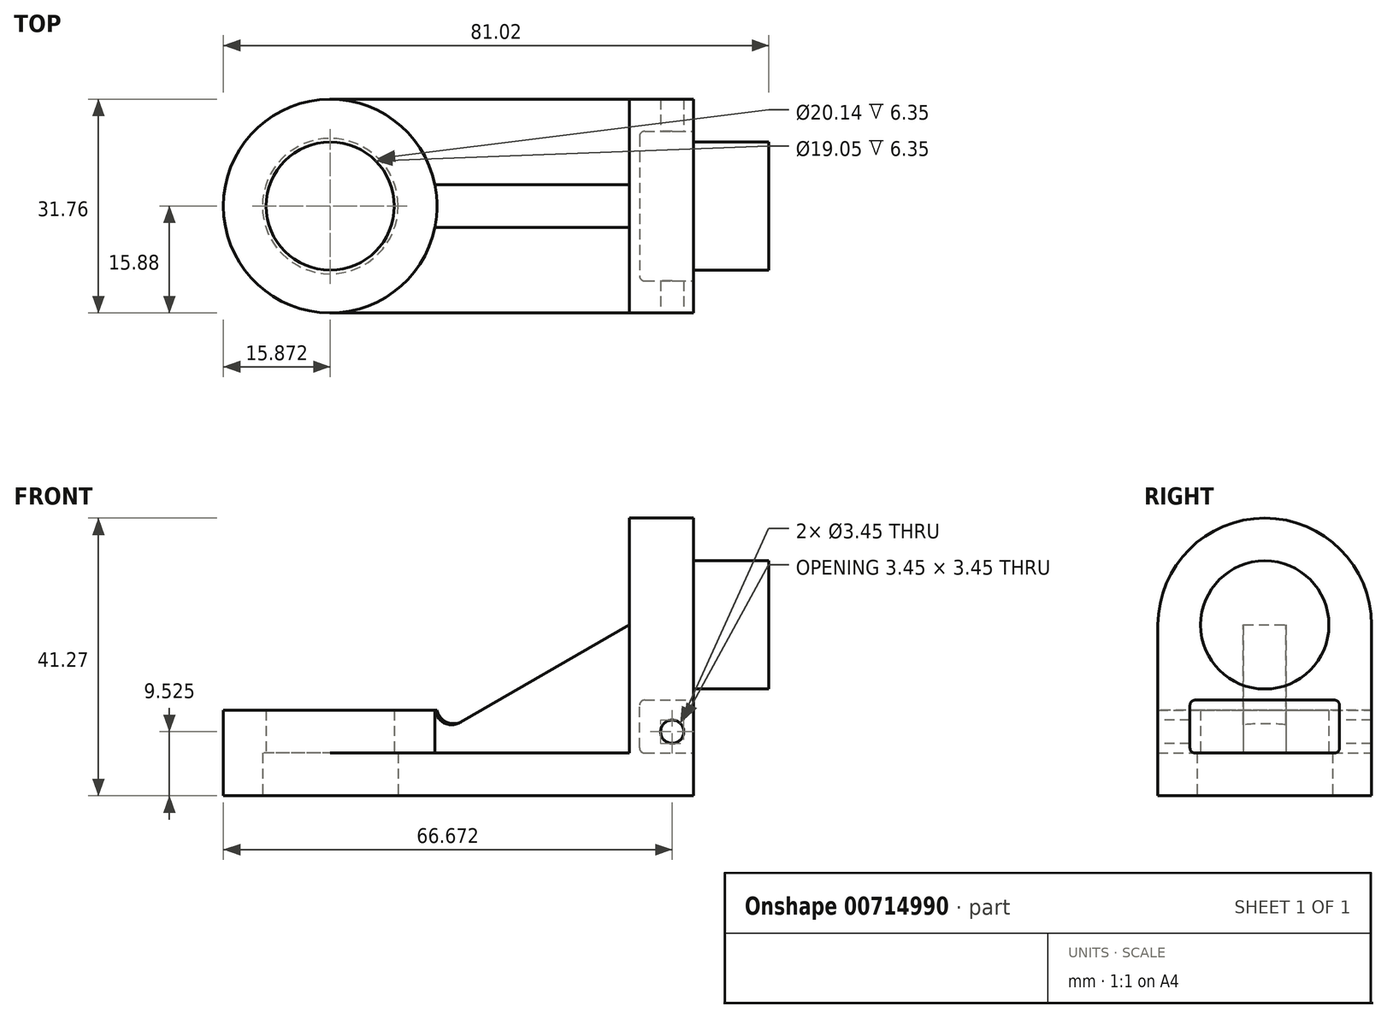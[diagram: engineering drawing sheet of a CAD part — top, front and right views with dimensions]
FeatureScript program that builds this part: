
annotation { "Feature Type Name" : "Feature", "Feature Type Description" : "" }
export const myFeature = defineFeature(function(context is Context, id is Id, definition is map)
    precondition{}
    {
        {
            var Q0;
            Q0=qCreatedBy(makeId("Top.planeOp"),FACE);
            var sketch = newSketch(context, id + "F0", { "sketchPlane" : qUnion([Q0])});
            skLineSegment(sketch, "E0.bottom", {"start": v(26.99, -15.88) * mm, "end": v(-26.99, -15.88) * mm});
            skLineSegment(sketch, "E0.top", {"start": v(26.99, 15.88) * mm, "end": v(-26.99, 15.87) * mm});
            skLineSegment(sketch, "E0.left", {"start": v(26.99, -15.88) * mm, "end": v(26.99, 15.88) * mm});
            skPoint(sketch, "E0.middle", {"position": v(0, 0) * mm});
            skArc(sketch, "E1", {"start": v(-26.99, 15.87) * mm, "mid": v(-42.86, 0) * mm, "end": v(-26.99, -15.87) * mm});
            skCircle(sketch, "E2", {"center": v(-26.99, 0) * mm, "radius": 10.07 * mm});
            skSolve(sketch);
        }
        {
            var Q0;
            Q0 = qSketchRegion(id + "F0", true);
            extrude(context, id + "F1", {"entities" : qUnion([Q0]), "depth" : 6.35 * mm, "offsetDistance" : 25.4 * mm});
        }
        {
            var Q0;
            Q0=makeQuery(id+"F1.opExtrude","CAP_FACE",FACE,{"disambiguationData":[OSD([sQuery(id+"F0.wireOp",EDGE,"E0.bottom"),sQuery(id+"F0.wireOp",EDGE,"E0.top"),sQuery(id+"F0.wireOp",EDGE,"E0.left"),sQuery(id+"F0.wireOp",EDGE,"E1")])],"isStart":false});
            var sketch = newSketch(context, id + "F2", { "sketchPlane" : qUnion([Q0])});
            skCircle(sketch, "E3", {"center": v(-26.99, 0) * mm, "radius": 9.53 * mm});
            skCircle(sketch, "E4", {"center": v(-26.99, 0) * mm, "radius": 15.88 * mm});
            skSolve(sketch);
        }
        {
            var Q0;
            Q0 = qSketchRegion(id + "F2", true);
            extrude(context, id + "F3", {"entities" : qUnion([Q0]), "operationType" : NewBodyOperationType.ADD, "depth" : 6.35 * mm, "offsetDistance" : 25.4 * mm});
        }
        {
            var Q0;
            Q0=makeQuery(id+"F1.opExtrude","CAP_FACE",FACE,{"disambiguationData":[OSD([sQuery(id+"F0.wireOp",EDGE,"E0.bottom"),sQuery(id+"F0.wireOp",EDGE,"E0.top"),sQuery(id+"F0.wireOp",EDGE,"E0.left"),sQuery(id+"F0.wireOp",EDGE,"E1"),sQuery(id+"F0.wireOp",EDGE,"E2")])],"isStart":false});
            var sketch = newSketch(context, id + "F4", { "sketchPlane" : qUnion([Q0])});
            skLineSegment(sketch, "E5.bottom", {"start": v(26.99, 15.88) * mm, "end": v(17.46, 15.88) * mm});
            skLineSegment(sketch, "E5.top", {"start": v(26.99, -15.88) * mm, "end": v(17.46, -15.88) * mm});
            skLineSegment(sketch, "E5.left", {"start": v(26.99, 15.88) * mm, "end": v(26.99, -15.88) * mm});
            skLineSegment(sketch, "E5.right", {"start": v(17.46, 15.88) * mm, "end": v(17.46, -15.88) * mm});
            skSolve(sketch);
        }
        {
            var Q0;
            Q0 = qSketchRegion(id + "F4", true);
            extrude(context, id + "F5", {"entities" : qUnion([Q0]), "operationType" : NewBodyOperationType.ADD, "depth" : 19.05 * mm, "offsetDistance" : 25.4 * mm});
        }
        {
            var Q0;
            Q0=makeQuery(id+"F5.boolean.opBoolean","MERGE",FACE,{"derivedFrom":[makeQuery(id+"F1.opExtrude","SWEPT_FACE",FACE,{"disambiguationData":[OSD([sQuery(id+"F0.wireOp",EDGE,"E0.left")])]}),makeQuery(id+"F5.opExtrude","SWEPT_FACE",FACE,{"disambiguationData":[OSD([sQuery(id+"F4.wireOp",EDGE,"E5.left")])]})]});
            var sketch = newSketch(context, id + "F6", { "sketchPlane" : qUnion([Q0])});
            skArc(sketch, "E6", {"start": v(15.88, 25.4) * mm, "mid": v(0, 41.28) * mm, "end": v(-15.88, 25.4) * mm});
            skLineSegment(sketch, "E7", {"start": v(-15.88, 25.4) * mm, "end": v(15.88, 25.4) * mm});
            skSolve(sketch);
        }
        {
            var Q0;
            Q0 = qSketchRegion(id + "F6", true);
            extrude(context, id + "F7", {"entities" : qUnion([Q0]), "operationType" : NewBodyOperationType.ADD, "oppositeDirection" : true, "depth" : 9.52 * mm, "offsetDistance" : 25.4 * mm});
        }
        {
            var Q0;
            Q0=makeQuery(id+"F7.boolean.opBoolean","MERGE",FACE,{"derivedFrom":[makeQuery(id+"F5.boolean.opBoolean","MERGE",FACE,{"derivedFrom":[makeQuery(id+"F1.opExtrude","SWEPT_FACE",FACE,{"disambiguationData":[OSD([sQuery(id+"F0.wireOp",EDGE,"E0.left")])]}),makeQuery(id+"F5.opExtrude","SWEPT_FACE",FACE,{"disambiguationData":[OSD([sQuery(id+"F4.wireOp",EDGE,"E5.left")])]})]}),makeQuery(id+"F7.opExtrude","CAP_FACE",FACE,{"disambiguationData":[OSD([sQuery(id+"F6.wireOp",EDGE,"E6"),sQuery(id+"F6.wireOp",EDGE,"E7")])],"isStart":true})]});
            var sketch = newSketch(context, id + "F8", { "sketchPlane" : qUnion([Q0])});
            skCircle(sketch, "E8", {"center": v(0, 25.4) * mm, "radius": 9.53 * mm});
            skSolve(sketch);
        }
        {
            var Q0;
            Q0 = qSketchRegion(id + "F8", true);
            extrude(context, id + "F9", {"entities" : qUnion([Q0]), "operationType" : NewBodyOperationType.ADD, "depth" : 11.18 * mm, "offsetDistance" : 25.4 * mm});
        }
        {
            var Q0;
            Q0=qCreatedBy(makeId("Front.planeOp"),FACE);
            var sketch = newSketch(context, id + "F10", { "sketchPlane" : qUnion([Q0])});
            skLineSegment(sketch, "E9.1", {"start": v(17.46, 6.35) * mm, "end": v(-13.33, 6.35) * mm});
            skPoint(sketch, "E9.2", {"position": v(-4.76, 6.35) * mm});
            skLineSegment(sketch, "E10", {"start": v(-13.39, 7.59) * mm, "end": v(17.46, 25.4) * mm});
            skLineSegment(sketch, "E11", {"start": v(17.46, 25.4) * mm, "end": v(17.46, 6.35) * mm});
            skPoint(sketch, "E9.0.end.orphan", {"position": v(17.46, 41.28) * mm});
            skPoint(sketch, "E12.orphan", {"position": v(-26.99, 6.35) * mm});
            skPoint(sketch, "E13.0.start.orphan", {"position": v(-42.86, 12.7) * mm});
            skPoint(sketch, "E14.orphan", {"position": v(-11.11, 12.7) * mm});
            skLineSegment(sketch, "E15", {"start": v(-13.39, 7.59) * mm, "end": v(-13.33, 6.35) * mm});
            skSolve(sketch);
        }
        {
            var Q0;
            Q0 = qSketchRegion(id + "F10", true);
            extrude(context, id + "F11", {"entities" : qUnion([Q0]), "operationType" : NewBodyOperationType.ADD, "endBound" : BoundingType.SYMMETRIC, "depth" : 6.35 * mm, "offsetDistance" : 25.4 * mm});
        }
        {
            var Q0;
            Q0=makeQuery(id+"F11.boolean.opBoolean","INTERSECT",EDGE,{"derivedFrom":[makeQuery(id+"F3.boolean.opBoolean","MERGE",FACE,{"derivedFrom":[makeQuery(id+"F1.opExtrude","SWEPT_FACE",FACE,{"disambiguationData":[OSD([sQuery(id+"F0.wireOp",EDGE,"E1")])]}),makeQuery(id+"F3.opExtrude","SWEPT_FACE",FACE,{"disambiguationData":[OSD([sQuery(id+"F2.wireOp",EDGE,"E4")])]})]}),makeQuery(id+"F11.opExtrude","SWEPT_FACE",FACE,{"disambiguationData":[OSD([sQuery(id+"F10.wireOp",EDGE,"E10")])]})]});
            fillet(context, id + "F12", {"entities" : qUnion([Q0]), "radius" : 2.54 * mm, "tangentPropagation" : true, "allowEdgeOverflow" : false});
        }
        {
            var Q0;
            Q0=makeQuery(id+"F7.boolean.opBoolean","MERGE",FACE,{"derivedFrom":[makeQuery(id+"F5.boolean.opBoolean","MERGE",FACE,{"derivedFrom":[makeQuery(id+"F1.opExtrude","SWEPT_FACE",FACE,{"disambiguationData":[OSD([sQuery(id+"F0.wireOp",EDGE,"E0.left")])]}),makeQuery(id+"F5.opExtrude","SWEPT_FACE",FACE,{"disambiguationData":[OSD([sQuery(id+"F4.wireOp",EDGE,"E5.left")])]})]}),makeQuery(id+"F7.opExtrude","CAP_FACE",FACE,{"disambiguationData":[OSD([sQuery(id+"F6.wireOp",EDGE,"E6"),sQuery(id+"F6.wireOp",EDGE,"E7")])],"isStart":true})]});
            var sketch = newSketch(context, id + "F13", { "sketchPlane" : qUnion([Q0])});
            skLineSegment(sketch, "E16.bottom", {"start": v(11.11, 6.35) * mm, "end": v(-11.11, 6.35) * mm});
            skLineSegment(sketch, "E16.top", {"start": v(11.11, 14.22) * mm, "end": v(-11.11, 14.22) * mm});
            skLineSegment(sketch, "E16.left", {"start": v(11.11, 6.35) * mm, "end": v(11.11, 14.22) * mm});
            skLineSegment(sketch, "E16.right", {"start": v(-11.11, 6.35) * mm, "end": v(-11.11, 14.22) * mm});
            skPoint(sketch, "E16.middle", {"position": v(0, 10.29) * mm});
            skSolve(sketch);
        }
        {
            var Q0;
            Q0 = qSketchRegion(id + "F13", true);
            extrude(context, id + "F14", {"entities" : qUnion([Q0]), "operationType" : NewBodyOperationType.REMOVE, "oppositeDirection" : true, "depth" : 8.03 * mm, "offsetDistance" : 25.4 * mm});
        }
        {
            var Q0;
            Q0=makeQuery(id+"F14.boolean.opBoolean","COPY",FACE,{"derivedFrom":makeQuery(id+"F14.opExtrude","CAP_FACE",FACE,{"disambiguationData":[OSD([sQuery(id+"F13.wireOp",EDGE,"E16.bottom"),sQuery(id+"F13.wireOp",EDGE,"E16.top"),sQuery(id+"F13.wireOp",EDGE,"E16.left"),sQuery(id+"F13.wireOp",EDGE,"E16.right")])],"isStart":false})});
            var Q1;
            Q1=makeQuery(id+"F14.boolean.opBoolean","COPY",EDGE,{"derivedFrom":makeQuery(id+"F14.opExtrude","SWEPT_EDGE",EDGE,{"disambiguationData":[OSD([sQuery(id+"F13.wireOp",EDGE,"E16.top"),sQuery(id+"F13.wireOp",EDGE,"E16.right")])]})});
            var Q2;
            Q2=makeQuery(id+"F14.boolean.opBoolean","COPY",EDGE,{"derivedFrom":makeQuery(id+"F14.opExtrude","SWEPT_EDGE",EDGE,{"disambiguationData":[OSD([sQuery(id+"F13.wireOp",EDGE,"E16.bottom"),sQuery(id+"F13.wireOp",EDGE,"E16.right")])]})});
            var Q3;
            Q3=makeQuery(id+"F14.boolean.opBoolean","COPY",EDGE,{"derivedFrom":makeQuery(id+"F14.opExtrude","SWEPT_EDGE",EDGE,{"disambiguationData":[OSD([sQuery(id+"F13.wireOp",EDGE,"E16.top"),sQuery(id+"F13.wireOp",EDGE,"E16.left")])]})});
            var Q4;
            Q4=makeQuery(id+"F14.boolean.opBoolean","COPY",EDGE,{"derivedFrom":makeQuery(id+"F14.opExtrude","SWEPT_EDGE",EDGE,{"disambiguationData":[OSD([sQuery(id+"F13.wireOp",EDGE,"E16.bottom"),sQuery(id+"F13.wireOp",EDGE,"E16.left")])]})});
            fillet(context, id + "F15", {"entities" : qUnion([Q0, Q1, Q2, Q3, Q4]), "radius" : 0.76 * mm, "tangentPropagation" : true, "allowEdgeOverflow" : false});
        }
        {
            var Q0;
            Q0=makeQuery(id+"F5.boolean.opBoolean","MERGE",FACE,{"derivedFrom":[makeQuery(id+"F1.opExtrude","SWEPT_FACE",FACE,{"disambiguationData":[OSD([sQuery(id+"F0.wireOp",EDGE,"E0.bottom")])]}),makeQuery(id+"F5.opExtrude","SWEPT_FACE",FACE,{"disambiguationData":[OSD([sQuery(id+"F4.wireOp",EDGE,"E5.top")])]})]});
            var sketch = newSketch(context, id + "F16", { "sketchPlane" : qUnion([Q0])});
            skCircle(sketch, "E17", {"center": v(23.81, 9.53) * mm, "radius": 1.73 * mm});
            skSolve(sketch);
        }
        {
            var Q0;
            Q0 = qSketchRegion(id + "F16", true);
            extrude(context, id + "F17", {"entities" : qUnion([Q0]), "operationType" : NewBodyOperationType.REMOVE, "endBound" : BoundingType.THROUGH_ALL, "oppositeDirection" : true, "depth" : 25.4 * mm, "offsetDistance" : 25.4 * mm});
        }
    });
